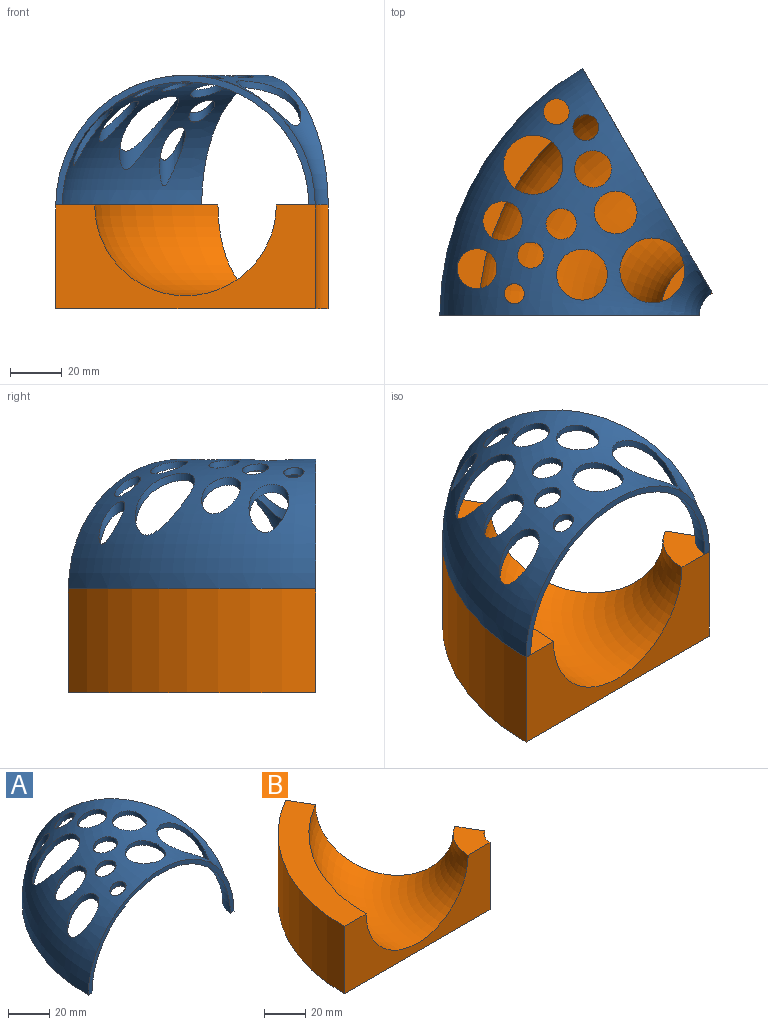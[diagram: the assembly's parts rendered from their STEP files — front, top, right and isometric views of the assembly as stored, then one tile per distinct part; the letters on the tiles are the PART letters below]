
ASSEMBLY  parts=2 mates=1
PART A: 18 faces, bbox 114.1x103.1x85.5 mm
  f0: torus R=60mm, axis (0,0,1), area 6949.5mm2, adj f2,f3,f4,f5,f6,f7,f8,f9
  f1: torus R=60mm, axis (0,0,1), area 6300.3mm2, adj f2,f3,f4,f5,f6,f7,f8,f9
  f2: plane 10.83x7.5mm, normal (0,0,-1), area 29.5mm2, adj f0,f1,f4,f5
  f3: plane 95.26x56.25mm, normal (0,0,-1), area 284.7mm2, adj f0,f1,f4,f5
  f4: plane 86.6x50mm, normal (0.87,0.5,0), area 382.9mm2, adj f0,f1,f2,f3
  f5: plane 100x50mm, normal (0,-1,0), area 382.9mm2, adj f0,f1,f2,f3
  f6: cylinder r=4.99mm len=26.34mm, axis (0,0,-1), area 180.1mm2, adj f0,f1
  f7: cylinder r=4.99mm len=11.24mm, axis (0,0,-1), area 101.2mm2, adj f0,f1
  f8: cylinder r=12.51mm len=25.02mm, axis (0,0,-1), area 245.8mm2, adj f0,f1
  f9: cylinder r=5.07mm len=10.14mm, axis (0,0,-1), area 86.5mm2, adj f0,f1
  f10: cylinder r=11.47mm len=30.94mm, axis (0,0,-1), area 298.3mm2, adj f0,f1
  f11: cylinder r=7.6mm len=18.57mm, axis (0,0,-1), area 171.5mm2, adj f0,f1
  f12: cylinder r=7.15mm len=14.3mm, axis (0,0,-1), area 120mm2, adj f0,f1
  f13: cylinder r=8.24mm len=16.48mm, axis (0,0,-1), area 130.5mm2, adj f0,f1
  f14: cylinder r=9.79mm len=19.58mm, axis (0,0,-1), area 155.6mm2, adj f0,f1
  f15: cylinder r=5.91mm len=11.82mm, axis (0,0,-1), area 96.5mm2, adj f0,f1
  f16: cylinder r=3.9mm len=7.79mm, axis (0,0,-1), area 68.6mm2, adj f0,f1
  f17: cylinder r=7.7mm len=25.13mm, axis (0,0,-1), area 210.7mm2, adj f0,f1
PART B: 8 faces, bbox 105x95.3x64.9 mm
  f0: plane 95.26x62.5mm, normal (0,0,1), area 1610.1mm2, adj f1,f5,f6,f7
  f1: cylinder r=110mm len=95.26mm, axis (0,0,1), area 4607.7mm2, adj f0,f2,f6,f7
  f2: plane 105x95.26mm, normal (0,0,-1), area 6283.2mm2, adj f1,f3,f6,f7
  f3: cylinder r=10mm len=40mm, axis (0,0,1), area 418.9mm2, adj f2,f4,f6,f7
  f4: plane 21.65x20mm, normal (0,0,1), area 274.9mm2, adj f3,f5,f6,f7
  f5: torus R=60mm, axis (0,0,1), area 6908.7mm2, adj f0,f4,f6,f7
  f6: plane 86.6x50mm, normal (0.87,0.5,0), area 2075.8mm2, adj f0,f1,f2,f3,f4,f5
  f7: plane 100x40mm, normal (0,-1,0), area 2075.8mm2, adj f0,f1,f2,f3,f4,f5
PLACE A t=(0,0,35.84)mm
PLACE B at identity
MATE fastened A.f0 <-> B.f1  axis (0,0,-1) through (60,0,20.33)mm
